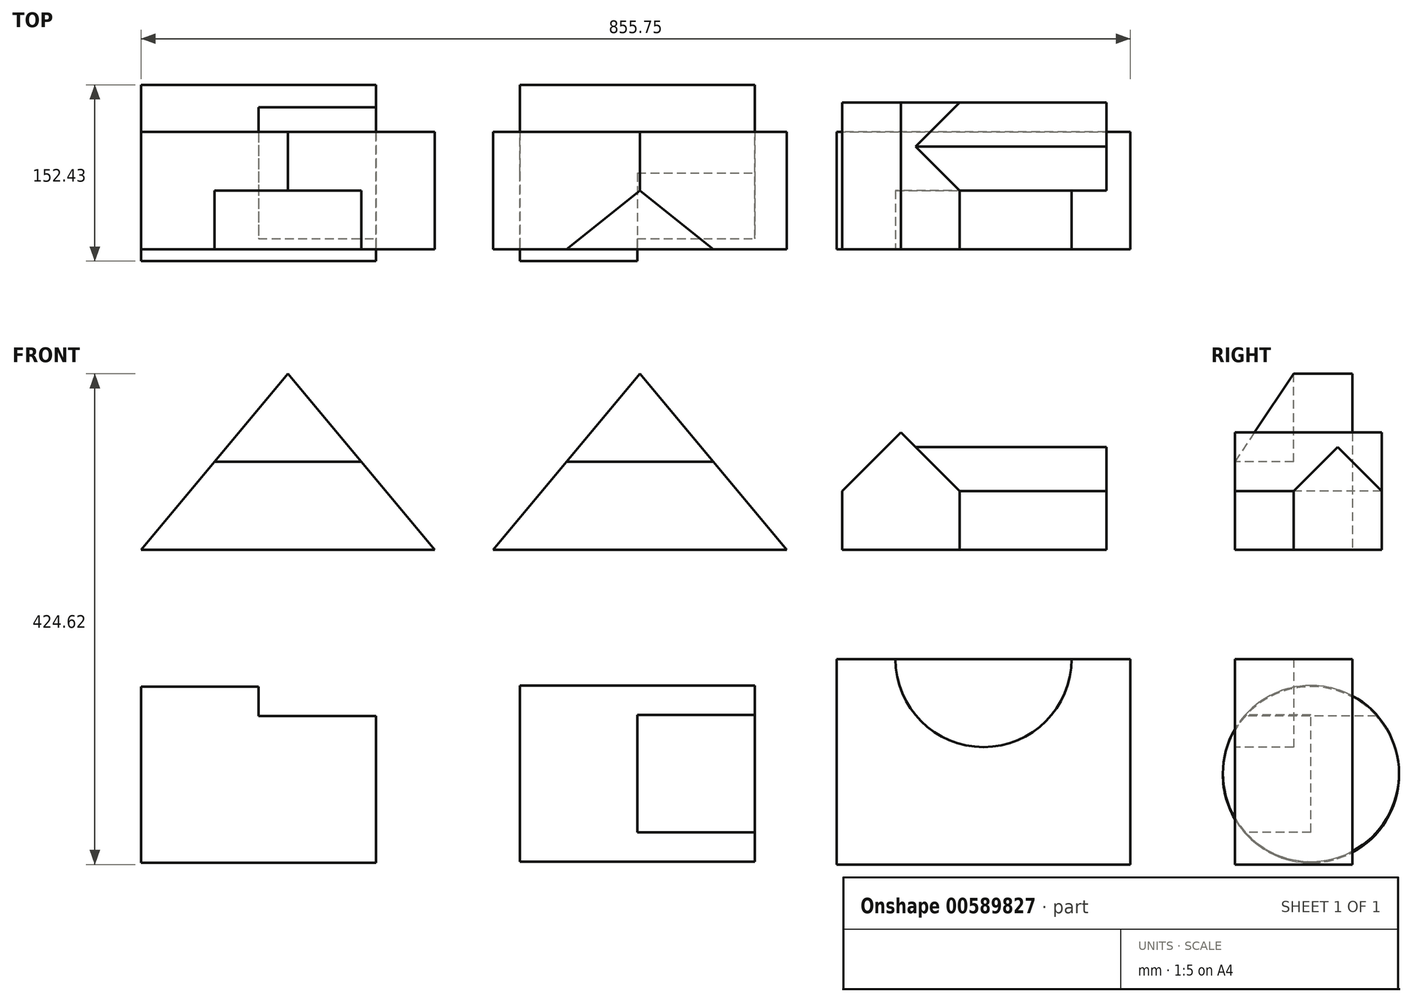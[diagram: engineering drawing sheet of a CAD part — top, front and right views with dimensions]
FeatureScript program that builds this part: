
annotation { "Feature Type Name" : "Feature", "Feature Type Description" : "" }
export const myFeature = defineFeature(function(context is Context, id is Id, definition is map)
    precondition{}
    {
        {
            var Q0;
            Q0=qCreatedBy(makeId("Front.planeOp"),FACE);
            var sketch = newSketch(context, id + "F0", { "sketchPlane" : qUnion([Q0])});
            skLineSegment(sketch, "E0", {"start": v(0, 0) * mm, "end": v(254, 0) * mm});
            skLineSegment(sketch, "E1", {"start": v(0, 0) * mm, "end": v(127, 152.4) * mm});
            skLineSegment(sketch, "E2", {"start": v(127, 152.4) * mm, "end": v(254, 0) * mm});
            skSolve(sketch);
        }
        {
            var Q0;
            Q0=makeQuery(id+"F0.imprint","IMPRINT",FACE,{"disambiguationData":[TD([[makeQuery(id+"F0.imprint","IMPRINT",EDGE,{"derivedFrom":sQuery(id+"F0.wireOp",EDGE,"E0")}),1.0]])]});
            extrude(context, id + "F1", {"entities" : qUnion([Q0]), "oppositeDirection" : true, "depth" : 101.6 * mm, "offsetDistance" : 25.4 * mm});
        }
        {
            var Q0;
            Q0=makeQuery(id+"F1.opExtrude","CAP_FACE",FACE,{"disambiguationData":[OSD([sQuery(id+"F0.wireOp",EDGE,"E0"),sQuery(id+"F0.wireOp",EDGE,"E1"),sQuery(id+"F0.wireOp",EDGE,"E2")])],"isStart":true});
            var sketch = newSketch(context, id + "F2", { "sketchPlane" : qUnion([Q0])});
            skLineSegment(sketch, "E3", {"start": v(127, 76.2) * mm, "end": v(63.5, 76.2) * mm});
            skLineSegment(sketch, "E4", {"start": v(63.5, 76.2) * mm, "end": v(190.5, 76.2) * mm});
            skSolve(sketch);
        }
        {
            var Q0;
            Q0 = qSketchRegion(id + "F2", true);
            var Q1;
            {var subQ0=sQuery(id+"F2.wireOp",EDGE,"E4");var subQ3=makeQuery(id+"F2.imprint","IMPRINT",VERTEX,{"derivedFrom":subQ0});Q1=makeQuery(id+"F2.imprint","IMPRINT",FACE,{"disambiguationData":[TD([[makeQuery(id+"F2.imprint","IMPRINT",EDGE,{"disambiguationData":[TD([[subQ3,1.0]])],"derivedFrom":subQ0}),1.0]])]});}
            extrude(context, id + "F3", {"entities" : qUnion([Q0, Q1]), "operationType" : NewBodyOperationType.REMOVE, "oppositeDirection" : true, "depth" : 50.8 * mm, "offsetDistance" : 25.4 * mm});
        }
        {
            var Q0;
            Q0=qCreatedBy(makeId("Front.planeOp"),FACE);
            var sketch = newSketch(context, id + "F4", { "sketchPlane" : qUnion([Q0])});
            skLineSegment(sketch, "E5", {"start": v(304.63, 0) * mm, "end": v(558.63, 0) * mm});
            skLineSegment(sketch, "E6", {"start": v(431.63, 152.4) * mm, "end": v(558.63, 0) * mm});
            skLineSegment(sketch, "E7", {"start": v(304.63, 0) * mm, "end": v(431.63, 152.4) * mm});
            skSolve(sketch);
        }
        {
            var Q0;
            Q0 = qSketchRegion(id + "F4", true);
            extrude(context, id + "F5", {"entities" : qUnion([Q0]), "oppositeDirection" : true, "depth" : 101.6 * mm, "offsetDistance" : 25.4 * mm});
        }
        {
            var Q0;
            Q0=makeQuery(id+"F5.opExtrude","CAP_EDGE",EDGE,{"disambiguationData":[OSD([sQuery(id+"F4.wireOp",EDGE,"E5")])],"isStart":true});
            cPoint(context, id + "F6", {"entities" : qUnion([Q0]), "parameter" : 0.5});
        }
        {
            var Q0;
            Q0=makeQuery(id+"F5.opExtrude","CAP_VERTEX",VERTEX,{"disambiguationData":[OSD([sQuery(id+"F4.wireOp",EDGE,"E6"),sQuery(id+"F4.wireOp",EDGE,"E7")])],"isStart":true});
            var Q1;
            Q1=makeQuery(id+"F5.opExtrude","CAP_VERTEX",VERTEX,{"disambiguationData":[OSD([sQuery(id+"F4.wireOp",EDGE,"E6"),sQuery(id+"F4.wireOp",EDGE,"E7")])],"isStart":false});
            var Q2;
            Q2 = qCreatedBy(id + "F6" ,VERTEX);
            cPlane(context, id + "F7", {"entities" : qUnion([Q0, Q1, Q2]), "cplaneType" : CPlaneType.THREE_POINT, "offset" : 25.4 * mm, "width" : 152.4 * mm, "height" : 152.4 * mm});
        }
        {
            var Q0;
            Q0=qCreatedBy(id+"F7.planeOp",FACE);
            var sketch = newSketch(context, id + "F8", { "sketchPlane" : qUnion([Q0])});
            skLineSegment(sketch, "E8", {"start": v(0, 152.4) * mm, "end": v(50.8, 152.4) * mm});
            skLineSegment(sketch, "E9", {"start": v(0, 152.4) * mm, "end": v(0, 76.2) * mm});
            skLineSegment(sketch, "E10", {"start": v(0, 76.2) * mm, "end": v(50.8, 152.4) * mm});
            skSolve(sketch);
        }
        {
            var Q0;
            Q0 = qSketchRegion(id + "F8", true);
            extrude(context, id + "F9", {"entities" : qUnion([Q0]), "operationType" : NewBodyOperationType.REMOVE, "endBound" : BoundingType.SYMMETRIC, "oppositeDirection" : true, "depth" : 127 * mm, "offsetDistance" : 25.4 * mm});
        }
        {
            var Q0;
            Q0=qCreatedBy(makeId("Front.planeOp"),FACE);
            var sketch = newSketch(context, id + "F10", { "sketchPlane" : qUnion([Q0])});
            skLineSegment(sketch, "E11", {"start": v(606.38, 0) * mm, "end": v(606.38, 50.8) * mm});
            skLineSegment(sketch, "E12", {"start": v(606.38, 0) * mm, "end": v(657.18, 0) * mm});
            skLineSegment(sketch, "E13", {"start": v(606.38, 50.8) * mm, "end": v(657.18, 101.6) * mm});
            skLineSegment(sketch, "E14", {"start": v(657.18, 0) * mm, "end": v(707.98, 0) * mm});
            skLineSegment(sketch, "E15", {"start": v(707.98, 0) * mm, "end": v(707.98, 50.8) * mm});
            skLineSegment(sketch, "E16", {"start": v(657.18, 101.6) * mm, "end": v(707.98, 50.8) * mm});
            skSolve(sketch);
        }
        {
            var Q0;
            Q0 = qSketchRegion(id + "F10", true);
            extrude(context, id + "F11", {"entities" : qUnion([Q0]), "oppositeDirection" : true, "depth" : 127 * mm, "offsetDistance" : 25.4 * mm});
        }
        {
            var Q0;
            Q0=makeQuery(id+"F11.opExtrude","SWEPT_FACE",FACE,{"disambiguationData":[OSD([sQuery(id+"F10.wireOp",EDGE,"E15")])]});
            cPlane(context, id + "F12", {"entities" : qUnion([Q0]), "cplaneType" : CPlaneType.OFFSET, "offset" : 127 * mm, "width" : 152.4 * mm, "height" : 152.4 * mm});
        }
        {
            var Q0;
            Q0=qCreatedBy(id+"F12.planeOp",FACE);
            var sketch = newSketch(context, id + "F13", { "sketchPlane" : qUnion([Q0])});
            skLineSegment(sketch, "E17", {"start": v(50.8, 50.8) * mm, "end": v(50.8, 0) * mm});
            skLineSegment(sketch, "E18", {"start": v(127, 0) * mm, "end": v(127, 50.8) * mm});
            skLineSegment(sketch, "E19", {"start": v(50.8, 50.8) * mm, "end": v(88.9, 88.9) * mm});
            skLineSegment(sketch, "E20", {"start": v(88.9, 88.9) * mm, "end": v(127, 50.8) * mm});
            skLineSegment(sketch, "E21", {"start": v(50.8, 0) * mm, "end": v(127, 0) * mm});
            skSolve(sketch);
        }
        {
            var Q0;
            Q0 = qSketchRegion(id + "F13", true);
            extrude(context, id + "F14", {"entities" : qUnion([Q0]), "operationType" : NewBodyOperationType.ADD, "endBound" : BoundingType.UP_TO_NEXT, "oppositeDirection" : true, "depth" : 127 * mm, "offsetDistance" : 25.4 * mm});
        }
        {
            var Q0;
            Q0=qCreatedBy(makeId("Right.planeOp"),FACE);
            var sketch = newSketch(context, id + "F15", { "sketchPlane" : qUnion([Q0])});
            skCircle(sketch, "E22", {"center": v(65.86, -194.55) * mm, "radius": 76.2 * mm});
            skSolve(sketch);
        }
        {
            var Q0;
            Q0=makeQuery(id+"F15.imprint","IMPRINT",FACE,{"disambiguationData":[TD([[makeQuery(id+"F15.imprint","IMPRINT",EDGE,{"derivedFrom":sQuery(id+"F15.wireOp",EDGE,"E22")}),1.0]])]});
            extrude(context, id + "F16", {"entities" : qUnion([Q0]), "depth" : 203.2 * mm, "offsetDistance" : 25.4 * mm});
        }
        {
            var Q0;
            Q0=makeQuery(id+"F16.opExtrude","CAP_FACE",FACE,{"disambiguationData":[OSD([sQuery(id+"F15.wireOp",EDGE,"E22")])],"isStart":false});
            var sketch = newSketch(context, id + "F17", { "sketchPlane" : qUnion([Q0])});
            skLineSegment(sketch, "E23", {"start": v(65.86, -143.75) * mm, "end": v(9.06, -143.75) * mm});
            skLineSegment(sketch, "E24", {"start": v(9.06, -143.75) * mm, "end": v(122.66, -143.75) * mm});
            skSolve(sketch);
        }
        {
            var Q0;
            {var subQ0=sQuery(id+"F17.wireOp",EDGE,"E24");var subQ3=makeQuery(id+"F17.imprint","IMPRINT",VERTEX,{"derivedFrom":subQ0});Q0=makeQuery(id+"F17.imprint","IMPRINT",FACE,{"disambiguationData":[TD([[makeQuery(id+"F17.imprint","IMPRINT",EDGE,{"disambiguationData":[TD([[subQ3,1.0]])],"derivedFrom":subQ0}),1.0]])]});}
            extrude(context, id + "F18", {"entities" : qUnion([Q0]), "operationType" : NewBodyOperationType.REMOVE, "oppositeDirection" : true, "depth" : 101.6 * mm, "offsetDistance" : 25.4 * mm});
        }
        {
            var Q0;
            Q0=qCreatedBy(makeId("Right.planeOp"),FACE);
            cPlane(context, id + "F19", {"entities" : qUnion([Q0]), "cplaneType" : CPlaneType.OFFSET, "offset" : 327.66 * mm, "width" : 152.4 * mm, "height" : 152.4 * mm});
        }
        {
            var Q0;
            Q0=qCreatedBy(id+"F19.planeOp",FACE);
            var sketch = newSketch(context, id + "F20", { "sketchPlane" : qUnion([Q0])});
            skCircle(sketch, "E25", {"center": v(65.9, -193.53) * mm, "radius": 76.2 * mm});
            skSolve(sketch);
        }
        {
            var Q0;
            Q0=makeQuery(id+"F20.imprint","IMPRINT",FACE,{"disambiguationData":[TD([[makeQuery(id+"F20.imprint","IMPRINT",EDGE,{"derivedFrom":sQuery(id+"F20.wireOp",EDGE,"E25")}),1.0]])]});
            extrude(context, id + "F21", {"entities" : qUnion([Q0]), "depth" : 203.2 * mm, "offsetDistance" : 25.4 * mm});
        }
        {
            var Q0;
            Q0=makeQuery(id+"F21.opExtrude","CAP_FACE",FACE,{"disambiguationData":[OSD([sQuery(id+"F20.wireOp",EDGE,"E25")])],"isStart":false});
            var sketch = newSketch(context, id + "F22", { "sketchPlane" : qUnion([Q0])});
            skLineSegment(sketch, "E26", {"start": v(65.9, -142.73) * mm, "end": v(9.1, -142.73) * mm});
            skLineSegment(sketch, "E27", {"start": v(65.9, -244.33) * mm, "end": v(9.1, -244.33) * mm});
            skLineSegment(sketch, "E28", {"start": v(65.9, -244.33) * mm, "end": v(65.9, -142.73) * mm});
            skSolve(sketch);
        }
        {
            var Q0;
            {var subQ0=sQuery(id+"F22.wireOp",EDGE,"E26");Q0=makeQuery(id+"F22.imprint","IMPRINT",FACE,{"disambiguationData":[TD([[makeQuery(id+"F22.imprint","IMPRINT",EDGE,{"derivedFrom":subQ0}),1.0]])]});}
            extrude(context, id + "F23", {"entities" : qUnion([Q0]), "operationType" : NewBodyOperationType.REMOVE, "oppositeDirection" : true, "depth" : 101.6 * mm, "offsetDistance" : 25.4 * mm});
        }
        {
            var Q0;
            Q0=qCreatedBy(makeId("Front.planeOp"),FACE);
            var sketch = newSketch(context, id + "F24", { "sketchPlane" : qUnion([Q0])});
            skLineSegment(sketch, "E29", {"start": v(601.75, -272.22) * mm, "end": v(855.75, -272.22) * mm});
            skLineSegment(sketch, "E30", {"start": v(855.75, -272.22) * mm, "end": v(855.75, -94.42) * mm});
            skLineSegment(sketch, "E31", {"start": v(855.75, -94.42) * mm, "end": v(804.95, -94.42) * mm});
            skLineSegment(sketch, "E32", {"start": v(601.75, -272.22) * mm, "end": v(601.75, -94.42) * mm});
            skLineSegment(sketch, "E33", {"start": v(601.75, -94.42) * mm, "end": v(652.55, -94.42) * mm});
            skLineSegment(sketch, "E34", {"start": v(652.55, -94.42) * mm, "end": v(855.75, -94.42) * mm});
            skSolve(sketch);
        }
        {
            var Q0;
            Q0=makeQuery(id+"F24.imprint","IMPRINT",FACE,{"disambiguationData":[TD([[makeQuery(id+"F24.imprint","IMPRINT",EDGE,{"derivedFrom":sQuery(id+"F24.wireOp",EDGE,"E29")}),1.0]])]});
            extrude(context, id + "F25", {"entities" : qUnion([Q0]), "oppositeDirection" : true, "depth" : 101.6 * mm, "offsetDistance" : 25.4 * mm});
        }
        {
            var Q0;
            Q0=makeQuery(id+"F25.opExtrude","CAP_FACE",FACE,{"disambiguationData":[OSD([sQuery(id+"F24.wireOp",EDGE,"E29"),sQuery(id+"F24.wireOp",EDGE,"E30"),sQuery(id+"F24.wireOp",EDGE,"E32"),sQuery(id+"F24.wireOp",EDGE,"E33"),sQuery(id+"F24.wireOp",EDGE,"E34")])],"isStart":true});
            var sketch = newSketch(context, id + "F26", { "sketchPlane" : qUnion([Q0])});
            skLineSegment(sketch, "E35", {"start": v(601.75, -94.42) * mm, "end": v(652.55, -94.42) * mm});
            skLineSegment(sketch, "E36", {"start": v(855.75, -94.42) * mm, "end": v(804.95, -94.42) * mm});
            skArc(sketch, "E37", {"start": v(652.55, -94.42) * mm, "mid": v(728.75, -170.62) * mm, "end": v(804.95, -94.42) * mm});
            skSolve(sketch);
        }
        {
            var Q0;
            {var subQ0=sQuery(id+"F26.wireOp",EDGE,"E37");Q0=makeQuery(id+"F26.imprint","IMPRINT",FACE,{"disambiguationData":[TD([[makeQuery(id+"F26.imprint","IMPRINT",EDGE,{"derivedFrom":subQ0}),1.0]])]});}
            extrude(context, id + "F27", {"entities" : qUnion([Q0]), "operationType" : NewBodyOperationType.REMOVE, "oppositeDirection" : true, "depth" : 50.8 * mm, "offsetDistance" : 25.4 * mm});
        }
    });
